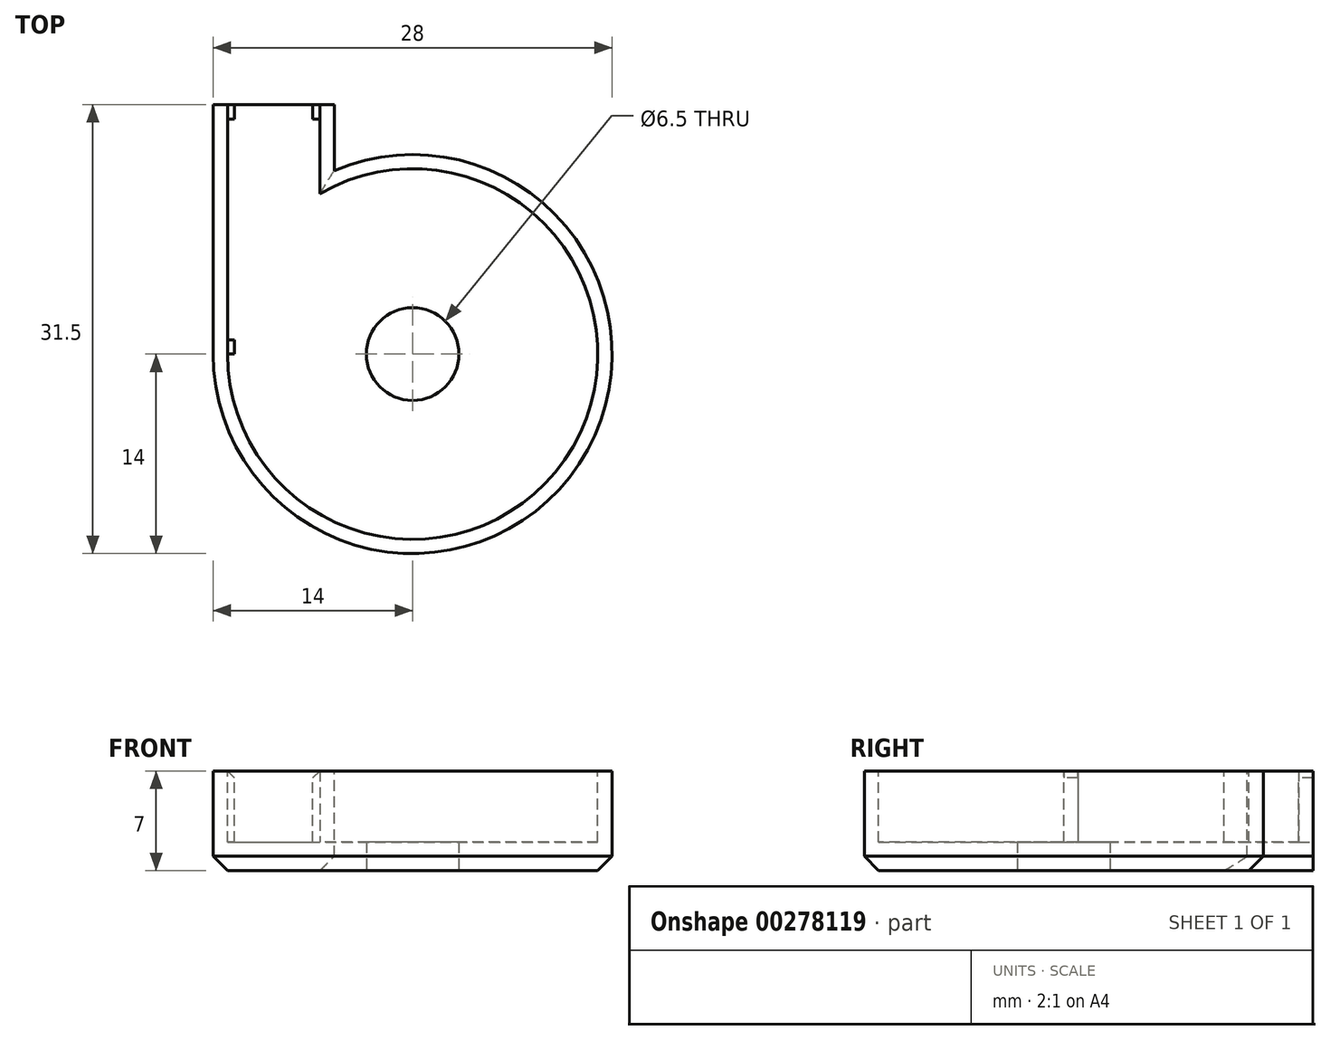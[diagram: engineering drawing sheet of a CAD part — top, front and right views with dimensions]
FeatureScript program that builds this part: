
annotation { "Feature Type Name" : "Feature", "Feature Type Description" : "" }
export const myFeature = defineFeature(function(context is Context, id is Id, definition is map)
    precondition{}
    {
        {
            var Q0;
            Q0=qCreatedBy(makeId("Top.planeOp"),FACE);
            var sketch = newSketch(context, id + "F0", { "sketchPlane" : qUnion([Q0])});
            skCircle(sketch, "E0", {"center": v(0, 0) * mm, "radius": 14 * mm});
            skCircle(sketch, "E1", {"center": v(0, 0) * mm, "radius": 3.25 * mm});
            skSolve(sketch);
        }
        {
            var Q0;
            Q0 = qSketchRegion(id + "F0", true);
            extrude(context, id + "F1", {"entities" : qUnion([Q0]), "depth" : 7 * mm});
        }
        {
            var Q0;
            Q0=makeQuery(id+"F1.opExtrude","CAP_FACE",FACE,{"disambiguationData":[OSD([sQuery(id+"F0.wireOp",EDGE,"E0")])],"isStart":false});
            var sketch = newSketch(context, id + "F2", { "sketchPlane" : qUnion([Q0])});
            skCircle(sketch, "E2", {"center": v(0, 0) * mm, "radius": 13 * mm});
            skSolve(sketch);
        }
        {
            var Q0;
            Q0 = qSketchRegion(id + "F2", true);
            extrude(context, id + "F3", {"entities" : qUnion([Q0]), "operationType" : NewBodyOperationType.REMOVE, "oppositeDirection" : true, "depth" : 5 * mm});
        }
        {
            var Q0;
            Q0=makeQuery(id+"F1.opExtrude","CAP_FACE",FACE,{"disambiguationData":[OSD([sQuery(id+"F0.wireOp",EDGE,"E0"),sQuery(id+"F0.wireOp",EDGE,"E1")])],"isStart":false});
            var sketch = newSketch(context, id + "F4", { "sketchPlane" : qUnion([Q0])});
            skLineSegment(sketch, "E3", {"start": v(-14, 0) * mm, "end": v(-14, 17.5) * mm});
            skLineSegment(sketch, "E4", {"start": v(-14, 17.5) * mm, "end": v(-5.5, 17.5) * mm});
            skLineSegment(sketch, "E5", {"start": v(-5.5, 17.5) * mm, "end": v(-5.5, 12.87) * mm});
            skLineSegment(sketch, "E6", {"start": v(-13, 0) * mm, "end": v(-13, 17.5) * mm});
            skLineSegment(sketch, "E7", {"start": v(-5.5, 17.5) * mm, "end": v(-6.5, 17.5) * mm});
            skLineSegment(sketch, "E8", {"start": v(-6.5, 17.5) * mm, "end": v(-6.5, 12.4) * mm});
            skSolve(sketch);
        }
        {
            var Q0;
            {var subQ0=sQuery(id+"F4.wireOp",EDGE,"E3");Q0=makeQuery(id+"F4.imprint","IMPRINT",FACE,{"disambiguationData":[TD([[makeQuery(id+"F4.imprint","IMPRINT",EDGE,{"derivedFrom":subQ0}),-1.0]])]});}
            var Q1;
            {var subQ0=sQuery(id+"F4.wireOp",EDGE,"E5");Q1=makeQuery(id+"F4.imprint","IMPRINT",FACE,{"disambiguationData":[TD([[makeQuery(id+"F4.imprint","IMPRINT",EDGE,{"derivedFrom":subQ0}),-1.0]])]});}
            extrude(context, id + "F5", {"entities" : qUnion([Q0, Q1]), "operationType" : NewBodyOperationType.ADD, "oppositeDirection" : true, "depth" : 7 * mm});
        }
        {
            var Q0;
            Q0=makeQuery(id+"F5.opExtrude","SWEPT_FACE",FACE,{"disambiguationData":[OSD([sQuery(id+"F4.wireOp",EDGE,"E4")])]});
            var sketch = newSketch(context, id + "F6", { "sketchPlane" : qUnion([Q0])});
            skLineSegment(sketch, "E9.bottom", {"start": v(14, 0) * mm, "end": v(5.5, 0) * mm});
            skLineSegment(sketch, "E9.top", {"start": v(14, 2) * mm, "end": v(5.5, 2) * mm});
            skLineSegment(sketch, "E9.left", {"start": v(14, 0) * mm, "end": v(14, 2) * mm});
            skLineSegment(sketch, "E9.right", {"start": v(5.5, 0) * mm, "end": v(5.5, 2) * mm});
            skSolve(sketch);
        }
        {
            var Q0;
            Q0 = qSketchRegion(id + "F6", true);
            extrude(context, id + "F7", {"entities" : qUnion([Q0]), "operationType" : NewBodyOperationType.ADD, "oppositeDirection" : true, "depth" : 12.8 * mm});
        }
        {
            var Q0;
            Q0=makeQuery(id+"F7.boolean.opBoolean","MERGE",FACE,{"derivedFrom":[makeQuery(id+"F5.opExtrude","SWEPT_FACE",FACE,{"disambiguationData":[OSD([sQuery(id+"F4.wireOp",EDGE,"E4")])]}),makeQuery(id+"F5.opExtrude","SWEPT_FACE",FACE,{"disambiguationData":[OSD([sQuery(id+"F4.wireOp",EDGE,"E7")])]}),makeQuery(id+"F7.opExtrude","CAP_FACE",FACE,{"disambiguationData":[OSD([sQuery(id+"F6.wireOp",EDGE,"E9.bottom"),sQuery(id+"F6.wireOp",EDGE,"E9.top"),sQuery(id+"F6.wireOp",EDGE,"E9.left"),sQuery(id+"F6.wireOp",EDGE,"E9.right")])],"isStart":true})]});
            var sketch = newSketch(context, id + "F8", { "sketchPlane" : qUnion([Q0])});
            skLineSegment(sketch, "E10.bottom", {"start": v(13, 7) * mm, "end": v(6.5, 7) * mm});
            skLineSegment(sketch, "E10.top", {"start": v(13, 2) * mm, "end": v(6.5, 2) * mm});
            skLineSegment(sketch, "E10.left", {"start": v(13, 7) * mm, "end": v(13, 2) * mm});
            skLineSegment(sketch, "E10.right", {"start": v(6.5, 7) * mm, "end": v(6.5, 2) * mm});
            skSolve(sketch);
        }
        {
            var Q0;
            Q0=makeQuery(id+"F8.imprint","IMPRINT",FACE,{"disambiguationData":[TD([[makeQuery(id+"F8.imprint","IMPRINT",EDGE,{"derivedFrom":sQuery(id+"F8.wireOp",EDGE,"E10.bottom")}),1.0]])]});
            extrude(context, id + "F9", {"entities" : qUnion([Q0]), "operationType" : NewBodyOperationType.REMOVE, "oppositeDirection" : true, "depth" : 17.5 * mm});
        }
        {
            var Q0;
            Q0=makeQuery(id+"F9.boolean.opBoolean","MERGE",FACE,{"derivedFrom":[makeQuery(id+"F5.opExtrude","SWEPT_FACE",FACE,{"disambiguationData":[OSD([sQuery(id+"F4.wireOp",EDGE,"E6")])]}),makeQuery(id+"F9.opExtrude","SWEPT_FACE",FACE,{"disambiguationData":[OSD([sQuery(id+"F8.wireOp",EDGE,"E10.left")])]})]});
            var sketch = newSketch(context, id + "F10", { "sketchPlane" : qUnion([Q0])});
            skLineSegment(sketch, "E11.bottom", {"start": v(0, 7) * mm, "end": v(1, 7) * mm});
            skLineSegment(sketch, "E11.top", {"start": v(0, 2) * mm, "end": v(1, 2) * mm});
            skLineSegment(sketch, "E11.left", {"start": v(0, 7) * mm, "end": v(0, 2) * mm});
            skLineSegment(sketch, "E11.right", {"start": v(1, 7) * mm, "end": v(1, 2) * mm});
            skLineSegment(sketch, "E12.bottom", {"start": v(17.5, 2) * mm, "end": v(16.5, 2) * mm});
            skLineSegment(sketch, "E12.top", {"start": v(17.5, 7) * mm, "end": v(16.5, 7) * mm});
            skLineSegment(sketch, "E12.left", {"start": v(17.5, 2) * mm, "end": v(17.5, 7) * mm});
            skLineSegment(sketch, "E12.right", {"start": v(16.5, 2) * mm, "end": v(16.5, 7) * mm});
            skSolve(sketch);
        }
        {
            var Q0;
            Q0 = qSketchRegion(id + "F10", true);
            extrude(context, id + "F11", {"entities" : qUnion([Q0]), "operationType" : NewBodyOperationType.ADD, "depth" : .5 * mm});
        }
        {
            var Q0;
            Q0=makeQuery(id+"F9.boolean.opBoolean","MERGE",FACE,{"derivedFrom":[makeQuery(id+"F5.opExtrude","SWEPT_FACE",FACE,{"disambiguationData":[OSD([sQuery(id+"F4.wireOp",EDGE,"E8")])]}),makeQuery(id+"F9.opExtrude","SWEPT_FACE",FACE,{"disambiguationData":[OSD([sQuery(id+"F8.wireOp",EDGE,"E10.right")])]})]});
            var sketch = newSketch(context, id + "F12", { "sketchPlane" : qUnion([Q0])});
            skLineSegment(sketch, "E13.bottom", {"start": v(-17.5, 7) * mm, "end": v(-16.5, 7) * mm});
            skLineSegment(sketch, "E13.top", {"start": v(-17.5, 2) * mm, "end": v(-16.5, 2) * mm});
            skLineSegment(sketch, "E13.left", {"start": v(-17.5, 7) * mm, "end": v(-17.5, 2) * mm});
            skLineSegment(sketch, "E13.right", {"start": v(-16.5, 7) * mm, "end": v(-16.5, 2) * mm});
            skSolve(sketch);
        }
        {
            var Q0;
            Q0 = qSketchRegion(id + "F12", true);
            extrude(context, id + "F13", {"entities" : qUnion([Q0]), "operationType" : NewBodyOperationType.ADD, "depth" : .5 * mm});
        }
        {
            var Q0;
            Q0=makeQuery(id+"F11.opExtrude","CAP_EDGE",EDGE,{"disambiguationData":[OSD([sQuery(id+"F10.wireOp",EDGE,"E11.bottom")])],"isStart":false});
            var Q1;
            Q1=makeQuery(id+"F11.opExtrude","CAP_EDGE",EDGE,{"disambiguationData":[OSD([sQuery(id+"F10.wireOp",EDGE,"E12.top")])],"isStart":false});
            var Q2;
            Q2=makeQuery(id+"F13.opExtrude","CAP_EDGE",EDGE,{"disambiguationData":[OSD([sQuery(id+"F12.wireOp",EDGE,"E13.bottom")])],"isStart":false});
            chamfer(context, id + "F14", {"entities" : qUnion([Q0, Q1, Q2]), "width" : .5 * mm, "tangentPropagation" : true});
        }
        {
            var Q0;
            {var subQ0=sQuery(id+"F4.wireOp",EDGE,"E3");var subQ1=sQuery(id+"F0.wireOp",EDGE,"E0");Q0=makeQuery(id+"F5.boolean.opBoolean","SPLIT",EDGE,{"disambiguationData":[TD([makeQuery(id+"F5.opExtrude","SWEPT_FACE",FACE,{"disambiguationData":[OSD([subQ0])]})])],"derivedFrom":makeQuery(id+"F1.opExtrude","CAP_EDGE",EDGE,{"disambiguationData":[OSD([subQ1])],"isStart":true})});}
            var Q1;
            Q1=makeQuery(id+"F5.opExtrude","CAP_EDGE",EDGE,{"disambiguationData":[OSD([sQuery(id+"F4.wireOp",EDGE,"E5")])],"isStart":false});
            var Q2;
            Q2=makeQuery(id+"F5.opExtrude","CAP_EDGE",EDGE,{"disambiguationData":[OSD([sQuery(id+"F4.wireOp",EDGE,"E3")])],"isStart":false});
            chamfer(context, id + "F15", {"entities" : qUnion([Q0, Q1, Q2]), "width" : 1 * mm, "tangentPropagation" : true});
        }
    });
